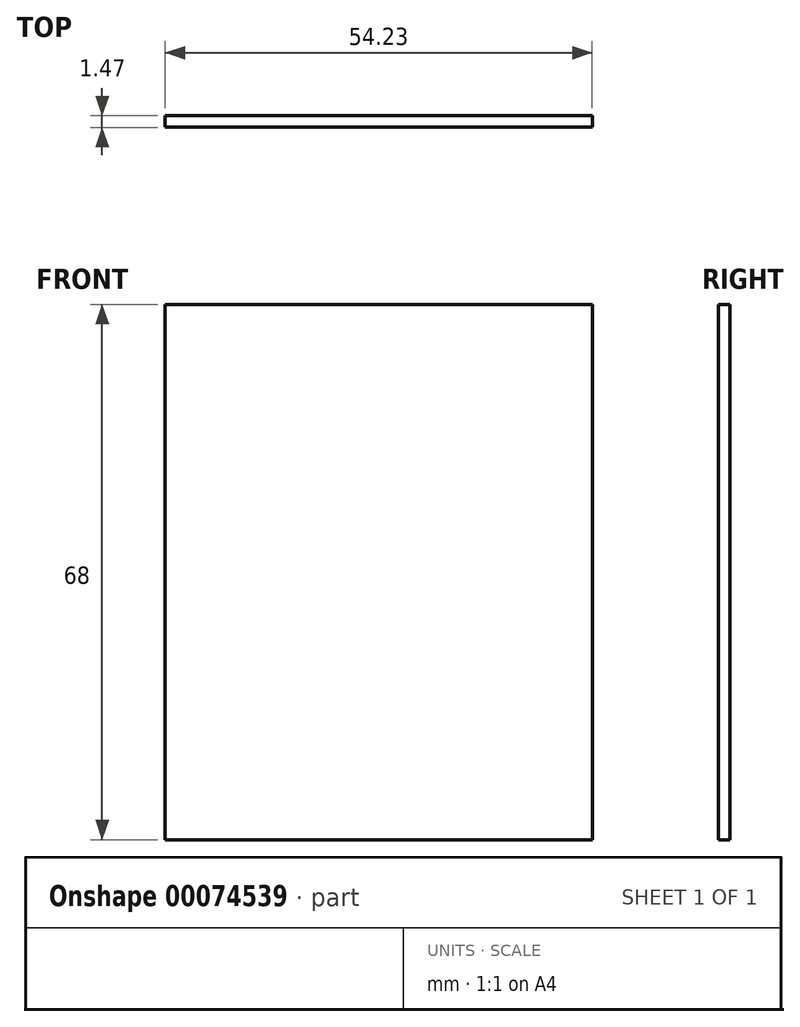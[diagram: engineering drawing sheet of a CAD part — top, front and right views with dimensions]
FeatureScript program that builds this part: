
annotation { "Feature Type Name" : "Feature", "Feature Type Description" : "" }
export const myFeature = defineFeature(function(context is Context, id is Id, definition is map)
    precondition{}
    {
        {
            var Q0;
            Q0=qCreatedBy(makeId("Top.planeOp"),FACE);
            var sketch = newSketch(context, id + "F0", { "sketchPlane" : qUnion([Q0])});
            skLineSegment(sketch, "E0.bottom", {"start": v(-6.87, -10.24) * mm, "end": v(47.36, -10.24) * mm});
            skLineSegment(sketch, "E0.top", {"start": v(-6.87, -11.7) * mm, "end": v(47.36, -11.7) * mm});
            skLineSegment(sketch, "E0.left", {"start": v(-6.87, -10.24) * mm, "end": v(-6.87, -11.7) * mm});
            skLineSegment(sketch, "E0.right", {"start": v(47.36, -10.24) * mm, "end": v(47.36, -11.7) * mm});
            skSolve(sketch);
        }
        {
            var Q0;
            Q0 = qSketchRegion(id + "F0", true);
            extrude(context, id + "F1", {"entities" : qUnion([Q0]), "depth" : 68 * mm});
        }
    });
